# Revit family: Lighting-Teknion-BLED_Linear_LED_Light-R2018
name_source: partatom
category: Lighting Fixtures
revit_build: Autodesk Revit 2018 (Build: 20190510_1515(x64)
units: mm (PartAtom-declared; Revit-internal decimal feet)

## family parameters
Always vertical = Yes
Cut with Voids When Loaded = No
Light Source = Yes
OmniClass Number = 23.80.70.00
OmniClass Title = Lighting
Part Type = Normal
Room Calculation Point = No
Round Connector Dimension = Use Diameter
Shared = No
Work Plane-Based = No

## types (3) — shared parameters
Color Filter = 16777215
Dimming Lamp Color Temperature Shift = <None>
Light Source Symbol Size = 24 "
Manufacturer = Teknion
Manufacturer Fax = 416.661.4586
Part Number = BLED
Product Documentation Link = https://www.teknion.com
Product Line = Expansion Casegoods
Product Page URL = https://www.teknion.com
Series = Expansion Casegoods
URL = www.teknion.com
Warranty = http://www.teknion.com

## per-type parameters (varying)
| type | Description | Emit from Line Length | Model | Width |
| 24" Width | Linear LED Light, 24" Width | 24 " | BLED24 | 22.953 " |
| 36" Width | Linear LED Light, 36" Width | 34 " | BLED36 | 34.953 " |
| 48" Width | Linear LED Light, 48" Width | 46 " | BLED48 | 46.953 " |

## geometry (parser evidence)
native form markers: Sweep x3
no freeform markers — native parametric forms only
